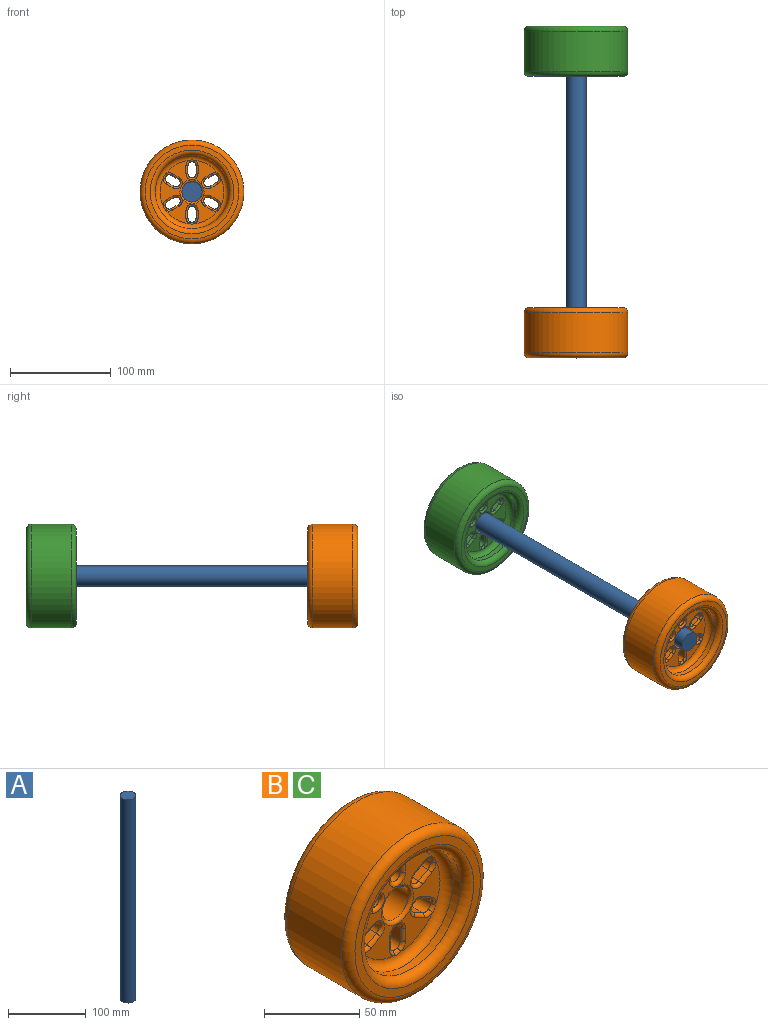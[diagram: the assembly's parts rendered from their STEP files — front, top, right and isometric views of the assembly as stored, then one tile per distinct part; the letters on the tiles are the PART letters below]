
ASSEMBLY  parts=3 mates=2
PART A: 3 faces, bbox 20x20x320 mm
  f0: cylinder r=10mm len=320mm, axis (0,0,-1), area 20106.2mm2, adj f1,f2
  f1: plane 20x20mm, normal (0,0,1), area 314.2mm2, adj f0
  f2: plane 20x20mm, normal (0,0,-1), area 314.2mm2, adj f0
PART B: 112 faces, bbox 111.7x50x111.7 mm
  f0: bspline ~6.36x4.57mm, area 12.6mm2, adj f1,f2,f13,f91
  f1: torus R=6mm, axis (0,1,0), area 16.8mm2, adj f0,f3,f13,f90
  f2: torus R=6mm, axis (0,1,0), area 16.8mm2, adj f0,f4,f13,f90
  f3: cylinder r=2mm len=7.93mm, axis (-0.87,0,-0.5), area 25.1mm2, adj f1,f5,f12,f90
  f4: cylinder r=2mm len=7.93mm, axis (0.87,0,0.5), area 25.1mm2, adj f2,f5,f14,f90
  f5: torus R=6mm, axis (0,1,0), area 46.7mm2, adj f3,f4,f15,f90
  f6: torus R=6mm, axis (0,1,0), area 16.8mm2, adj f7,f8,f13,f86
  f7: bspline ~6.36x4.57mm, area 12.6mm2, adj f6,f9,f13,f85
  f8: cylinder r=2mm len=7.93mm, axis (0.87,0,0.5), area 25.1mm2, adj f6,f10,f12,f86
  f9: torus R=6mm, axis (0,1,0), area 16.8mm2, adj f7,f11,f13,f86
  f10: torus R=6mm, axis (0,1,0), area 46.7mm2, adj f8,f11,f15,f86
  f11: cylinder r=2mm len=7.93mm, axis (-0.87,0,-0.5), area 25.1mm2, adj f9,f10,f14,f86
  f12: plane 16x6.93mm, normal (0.5,0,-0.87), area 128mm2, adj f3,f8,f13,f15
  f13: cylinder r=4mm len=16mm, axis (0,1,0), area 201.1mm2, adj f0,f1,f2,f6,f7,f9,f12,f14
  f14: plane 16x6.93mm, normal (-0.5,0,0.87), area 128mm2, adj f4,f11,f13,f15
  f15: cylinder r=4mm len=16mm, axis (0,1,0), area 201.1mm2, adj f5,f10,f12,f14
  f16: bspline ~6.36x4.57mm, area 12.6mm2, adj f17,f18,f29,f91
  f17: torus R=6mm, axis (0,1,0), area 16.8mm2, adj f16,f19,f29,f90
  f18: torus R=6mm, axis (0,1,0), area 16.8mm2, adj f16,f20,f29,f90
  f19: cylinder r=2mm len=7.93mm, axis (-0.87,0,0.5), area 25.1mm2, adj f17,f21,f28,f90
  f20: cylinder r=2mm len=7.93mm, axis (0.87,0,-0.5), area 25.1mm2, adj f18,f21,f30,f90
  f21: torus R=6mm, axis (0,1,0), area 46.7mm2, adj f19,f20,f31,f90
  f22: torus R=6mm, axis (0,1,0), area 16.8mm2, adj f23,f24,f29,f86
  f23: bspline ~6.36x4.57mm, area 12.6mm2, adj f22,f25,f29,f85
  f24: cylinder r=2mm len=7.93mm, axis (0.87,0,-0.5), area 25.1mm2, adj f22,f26,f28,f86
  f25: torus R=6mm, axis (0,1,0), area 16.8mm2, adj f23,f27,f29,f86
  f26: torus R=6mm, axis (0,1,0), area 46.7mm2, adj f24,f27,f31,f86
  f27: cylinder r=2mm len=7.93mm, axis (-0.87,0,0.5), area 25.1mm2, adj f25,f26,f30,f86
  f28: plane 16x6.93mm, normal (-0.5,0,-0.87), area 128mm2, adj f19,f24,f29,f31
  f29: cylinder r=4mm len=16mm, axis (0,1,0), area 201.1mm2, adj f16,f17,f18,f22,f23,f25,f28,f30
  f30: plane 16x6.93mm, normal (0.5,0,0.87), area 128mm2, adj f20,f27,f29,f31
  f31: cylinder r=4mm len=16mm, axis (0,1,0), area 201.1mm2, adj f21,f26,f28,f30
  f32: bspline ~7.35x2.69mm, area 12.6mm2, adj f33,f34,f45,f91
  f33: torus R=6mm, axis (0,1,0), area 16.8mm2, adj f32,f35,f45,f90
  f34: torus R=6mm, axis (0,1,0), area 16.8mm2, adj f32,f36,f45,f90
  f35: cylinder r=2mm len=8mm, axis (0,0,1), area 25.1mm2, adj f33,f37,f44,f90
  f36: cylinder r=2mm len=8mm, axis (0,0,-1), area 25.1mm2, adj f34,f37,f46,f90
  f37: torus R=6mm, axis (0,1,0), area 46.7mm2, adj f35,f36,f47,f90
  f38: torus R=6mm, axis (0,1,0), area 16.8mm2, adj f39,f40,f45,f86
  f39: bspline ~7.35x2.69mm, area 12.6mm2, adj f38,f41,f45,f85
  f40: cylinder r=2mm len=8mm, axis (0,0,-1), area 25.1mm2, adj f38,f42,f44,f86
  f41: torus R=6mm, axis (0,1,0), area 16.8mm2, adj f39,f43,f45,f86
  f42: torus R=6mm, axis (0,1,0), area 46.7mm2, adj f40,f43,f47,f86
  f43: cylinder r=2mm len=8mm, axis (0,0,1), area 25.1mm2, adj f41,f42,f46,f86
  f44: plane 16x8mm, normal (-1,0,0), area 128mm2, adj f35,f40,f45,f47
  f45: cylinder r=4mm len=16mm, axis (0,1,0), area 201.1mm2, adj f32,f33,f34,f38,f39,f41,f44,f46
  f46: plane 16x8mm, normal (1,0,0), area 128mm2, adj f36,f43,f45,f47
  f47: cylinder r=4mm len=16mm, axis (0,1,0), area 201.1mm2, adj f37,f42,f44,f46
  f48: bspline ~6.36x4.57mm, area 12.6mm2, adj f49,f50,f61,f91
  f49: torus R=6mm, axis (0,1,0), area 16.8mm2, adj f48,f51,f61,f90
  f50: torus R=6mm, axis (0,1,0), area 16.8mm2, adj f48,f52,f61,f90
  f51: cylinder r=2mm len=7.93mm, axis (0.87,0,0.5), area 25.1mm2, adj f49,f53,f60,f90
  f52: cylinder r=2mm len=7.93mm, axis (-0.87,0,-0.5), area 25.1mm2, adj f50,f53,f62,f90
  f53: torus R=6mm, axis (0,1,0), area 46.7mm2, adj f51,f52,f63,f90
  f54: torus R=6mm, axis (0,1,0), area 16.8mm2, adj f55,f56,f61,f86
  f55: bspline ~6.36x4.57mm, area 12.6mm2, adj f54,f57,f61,f85
  f56: cylinder r=2mm len=7.93mm, axis (-0.87,0,-0.5), area 25.1mm2, adj f54,f58,f60,f86
  f57: torus R=6mm, axis (0,1,0), area 16.8mm2, adj f55,f59,f61,f86
  f58: torus R=6mm, axis (0,1,0), area 46.7mm2, adj f56,f59,f63,f86
  f59: cylinder r=2mm len=7.93mm, axis (0.87,0,0.5), area 25.1mm2, adj f57,f58,f62,f86
  f60: plane 16x6.93mm, normal (-0.5,0,0.87), area 128mm2, adj f51,f56,f61,f63
  f61: cylinder r=4mm len=16mm, axis (0,1,0), area 201.1mm2, adj f48,f49,f50,f54,f55,f57,f60,f62
  f62: plane 16x6.93mm, normal (0.5,0,-0.87), area 128mm2, adj f52,f59,f61,f63
  f63: cylinder r=4mm len=16mm, axis (0,1,0), area 201.1mm2, adj f53,f58,f60,f62
  f64: bspline ~6.36x4.57mm, area 12.6mm2, adj f65,f66,f77,f91
  f65: torus R=6mm, axis (0,1,0), area 16.8mm2, adj f64,f67,f77,f90
  f66: torus R=6mm, axis (0,1,0), area 16.8mm2, adj f64,f68,f77,f90
  f67: cylinder r=2mm len=7.93mm, axis (0.87,0,-0.5), area 25.1mm2, adj f65,f69,f76,f90
  f68: cylinder r=2mm len=7.93mm, axis (-0.87,0,0.5), area 25.1mm2, adj f66,f69,f78,f90
  f69: torus R=6mm, axis (0,1,0), area 46.7mm2, adj f67,f68,f79,f90
  f70: torus R=6mm, axis (0,1,0), area 16.8mm2, adj f71,f72,f77,f86
  f71: bspline ~6.36x4.57mm, area 12.6mm2, adj f70,f73,f77,f85
  f72: cylinder r=2mm len=7.93mm, axis (-0.87,0,0.5), area 25.1mm2, adj f70,f74,f76,f86
  f73: torus R=6mm, axis (0,1,0), area 16.8mm2, adj f71,f75,f77,f86
  f74: torus R=6mm, axis (0,1,0), area 46.7mm2, adj f72,f75,f79,f86
  f75: cylinder r=2mm len=7.93mm, axis (0.87,0,-0.5), area 25.1mm2, adj f73,f74,f78,f86
  f76: plane 16x6.93mm, normal (0.5,0,0.87), area 128mm2, adj f67,f72,f77,f79
  f77: cylinder r=4mm len=16mm, axis (0,1,0), area 201.1mm2, adj f64,f65,f66,f70,f71,f73,f76,f78
  f78: plane 16x6.93mm, normal (-0.5,0,-0.87), area 128mm2, adj f68,f75,f77,f79
  f79: cylinder r=4mm len=16mm, axis (0,1,0), area 201.1mm2, adj f69,f74,f76,f78
  f80: cylinder r=51.6mm len=103.2mm, axis (0,-1,0), area 12968.5mm2, adj f81,f95
  f81: torus R=46.6mm, axis (0,-1,0), area 2456.7mm2, adj f80,f82
  f82: plane 93.2x93.2mm, normal (0,-1,0), area 1385.4mm2, adj f81,f83
  f83: torus R=41.6mm, axis (0,-1,0), area 1895.8mm2, adj f82,f84
  f84: cylinder r=36.6mm len=73.2mm, axis (0,-1,0), area 1149.8mm2, adj f83,f85
  f85: torus R=31.6mm, axis (0,-1,0), area 1709.6mm2, adj f7,f23,f39,f55,f71,f84,f86,f101
  f86: plane 63.2x62.99mm, normal (0,-1,0), area 1439.8mm2, adj f6,f8,f9,f10,f11,f22,f24,f25
  f87: torus R=12mm, axis (0,-1,0), area 211.7mm2, adj f86,f88
  f88: cylinder r=10mm len=20mm, axis (0,-1,0), area 1005.3mm2, adj f87,f89
  f89: torus R=12mm, axis (0,-1,0), area 211.7mm2, adj f88,f90
  f90: plane 63.2x62.99mm, normal (0,1,0), area 1439.8mm2, adj f1,f2,f3,f4,f5,f17,f18,f19
  f91: torus R=31.6mm, axis (0,-1,0), area 1709.6mm2, adj f0,f16,f32,f48,f64,f90,f92,f106
  f92: cylinder r=36.6mm len=73.2mm, axis (0,-1,0), area 1149.8mm2, adj f91,f93
  f93: torus R=41.6mm, axis (0,-1,0), area 1895.8mm2, adj f92,f94
  f94: plane 93.2x93.2mm, normal (0,1,0), area 1385.4mm2, adj f93,f95
  f95: torus R=46.6mm, axis (0,-1,0), area 2456.7mm2, adj f80,f94
  f96: plane 16x8mm, normal (1,0,0), area 128mm2, adj f97,f99,f102,f109
  f97: cylinder r=4mm len=16mm, axis (0,1,0), area 201.1mm2, adj f96,f98,f100,f101,f103,f106,f107,f108
  f98: plane 16x8mm, normal (-1,0,0), area 128mm2, adj f97,f99,f105,f110
  f99: cylinder r=4mm len=16mm, axis (0,1,0), area 201.1mm2, adj f96,f98,f104,f111
  f100: torus R=6mm, axis (0,1,0), area 16.8mm2, adj f86,f97,f101,f102
  f101: bspline ~7.35x2.69mm, area 12.6mm2, adj f85,f97,f100,f103
  f102: cylinder r=2mm len=8mm, axis (0,0,1), area 25.1mm2, adj f86,f96,f100,f104
  f103: torus R=6mm, axis (0,1,0), area 16.8mm2, adj f86,f97,f101,f105
  f104: torus R=6mm, axis (0,1,0), area 46.7mm2, adj f86,f99,f102,f105
  f105: cylinder r=2mm len=8mm, axis (0,0,-1), area 25.1mm2, adj f86,f98,f103,f104
  f106: bspline ~7.35x2.69mm, area 12.6mm2, adj f91,f97,f107,f108
  f107: torus R=6mm, axis (0,1,0), area 16.8mm2, adj f90,f97,f106,f109
  f108: torus R=6mm, axis (0,1,0), area 16.8mm2, adj f90,f97,f106,f110
  f109: cylinder r=2mm len=8mm, axis (0,0,-1), area 25.1mm2, adj f90,f96,f107,f111
  f110: cylinder r=2mm len=8mm, axis (0,0,1), area 25.1mm2, adj f90,f98,f108,f111
  f111: torus R=6mm, axis (0,1,0), area 46.7mm2, adj f90,f99,f109,f110
PART C: same geometry as B
PLACE A rot(axis=(-1,0,0),90deg) t=(-100.54,26.96,127.51)mm fixed
PLACE B rot(axis=(1,0,0),0deg) t=(-100.54,46.96,127.51)mm
PLACE C t=(-100.54,326.96,127.51)mm
MATE fastened C.f80 <-> A.f0  axis (0,1,0) through (-100.54,336.96,127.51)mm
MATE fastened B.f80 <-> A.f0  axis (0,-1,0) through (-100.54,36.96,127.51)mm
